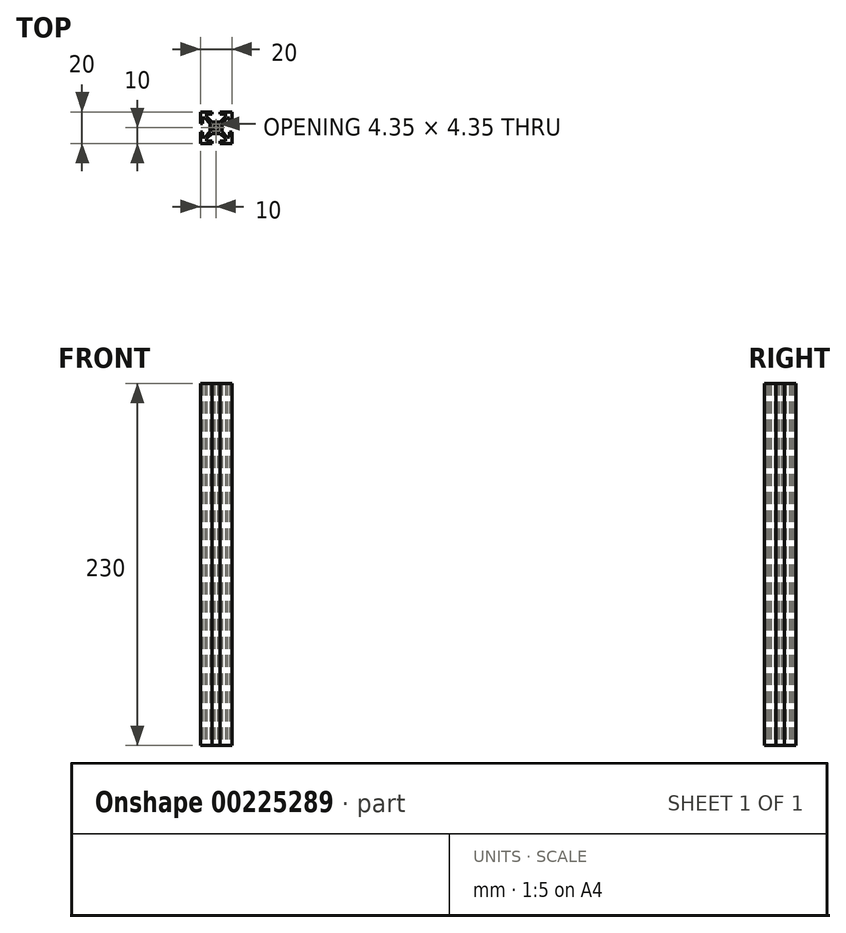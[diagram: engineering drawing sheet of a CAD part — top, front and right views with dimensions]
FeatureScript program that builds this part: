
annotation { "Feature Type Name" : "Feature", "Feature Type Description" : "" }
export const myFeature = defineFeature(function(context is Context, id is Id, definition is map)
    precondition{}
    {
        {
            var Q0;
            Q0=qCreatedBy(makeId("Top.planeOp"),FACE);
            var sketch = newSketch(context, id + "F0", { "sketchPlane" : qUnion([Q0])});
            skLineSegment(sketch, "E0.bottom", {"start": v(10, 10) * mm, "end": v(-10, 10) * mm});
            skLineSegment(sketch, "E0.top", {"start": v(10, -10) * mm, "end": v(-10, -10) * mm});
            skLineSegment(sketch, "E0.left", {"start": v(10, 10) * mm, "end": v(10, -10) * mm});
            skLineSegment(sketch, "E0.right", {"start": v(-10, 10) * mm, "end": v(-10, -10) * mm});
            skPoint(sketch, "E0.middle", {"position": v(0, 0) * mm});
            skLineSegment(sketch, "E1", {"start": v(-10, 10) * mm, "end": v(10, -10) * mm, "construction": true});
            skLineSegment(sketch, "E2", {"start": v(-10, -10) * mm, "end": v(10, 10) * mm, "construction": true});
            skLineSegment(sketch, "E3", {"start": v(0, 10) * mm, "end": v(0, -10) * mm, "construction": true});
            skLineSegment(sketch, "E4", {"start": v(-10, 0) * mm, "end": v(10, 0) * mm, "construction": true});
            skPoint(sketch, "E4.endSnap0", {"position": v(10, 0) * mm});
            skLineSegment(sketch, "E5", {"start": v(-2.63, 13.49) * mm, "end": v(2.63, 13.49) * mm});
            skLineSegment(sketch, "E6", {"start": v(2.63, 13.49) * mm, "end": v(2.63, 8.5) * mm});
            skLineSegment(sketch, "E7", {"start": v(2.63, 8.5) * mm, "end": v(6, 8.5) * mm});
            skLineSegment(sketch, "E8", {"start": v(6, 8.5) * mm, "end": v(6, 7.06) * mm});
            skLineSegment(sketch, "E9", {"start": v(6, 7.06) * mm, "end": v(2.6, 3.66) * mm});
            skLineSegment(sketch, "E10", {"start": v(2.6, 3.66) * mm, "end": v(-2.6, 3.66) * mm});
            skLineSegment(sketch, "E11", {"start": v(-2.6, 3.66) * mm, "end": v(-6, 7.06) * mm});
            skLineSegment(sketch, "E12", {"start": v(-6, 7.06) * mm, "end": v(-6, 8.5) * mm});
            skLineSegment(sketch, "E13", {"start": v(-6, 8.5) * mm, "end": v(-2.63, 8.5) * mm});
            skLineSegment(sketch, "E14", {"start": v(-2.63, 8.5) * mm, "end": v(-2.63, 13.49) * mm});
            skCircle(sketch, "E15", {"center": v(0, 0) * mm, "radius": 2.1 * mm});
            skLineSegment(sketch, "E16.MirrorCS", {"start": v(-7.06, 6) * mm, "end": v(-8.5, 6) * mm});
            skLineSegment(sketch, "E17.MirrorCS", {"start": v(-3.66, 2.6) * mm, "end": v(-7.06, 6) * mm});
            skLineSegment(sketch, "E18.MirrorCS", {"start": v(-8.5, 6) * mm, "end": v(-8.5, 2.63) * mm});
            skLineSegment(sketch, "E19.MirrorCS", {"start": v(-3.66, -2.6) * mm, "end": v(-3.66, 2.6) * mm});
            skLineSegment(sketch, "E20.MirrorCS", {"start": v(-7.06, -6) * mm, "end": v(-3.66, -2.6) * mm});
            skLineSegment(sketch, "E21.MirrorCS", {"start": v(-8.5, -6) * mm, "end": v(-7.06, -6) * mm});
            skLineSegment(sketch, "E22.MirrorCS", {"start": v(-8.5, -2.63) * mm, "end": v(-8.5, -6) * mm});
            skLineSegment(sketch, "E23.MirrorCS", {"start": v(-13.49, -2.63) * mm, "end": v(-8.5, -2.63) * mm});
            skLineSegment(sketch, "E24.MirrorCS", {"start": v(-13.49, 2.63) * mm, "end": v(-13.49, -2.63) * mm});
            skLineSegment(sketch, "E25.MirrorCS", {"start": v(-8.5, 2.63) * mm, "end": v(-13.49, 2.63) * mm});
            skLineSegment(sketch, "E26.MirrorCS", {"start": v(-2.6, -3.66) * mm, "end": v(-6, -7.06) * mm});
            skLineSegment(sketch, "E27.MirrorCS", {"start": v(2.6, -3.66) * mm, "end": v(-2.6, -3.66) * mm});
            skLineSegment(sketch, "E28.MirrorCS", {"start": v(6, -7.06) * mm, "end": v(2.6, -3.66) * mm});
            skLineSegment(sketch, "E29.MirrorCS", {"start": v(6, -8.5) * mm, "end": v(6, -7.06) * mm});
            skLineSegment(sketch, "E30.MirrorCS", {"start": v(2.63, -8.5) * mm, "end": v(6, -8.5) * mm});
            skLineSegment(sketch, "E31.MirrorCS", {"start": v(2.63, -13.49) * mm, "end": v(2.63, -8.5) * mm});
            skLineSegment(sketch, "E32.MirrorCS", {"start": v(-2.63, -13.49) * mm, "end": v(2.63, -13.49) * mm});
            skLineSegment(sketch, "E33.MirrorCS", {"start": v(-2.63, -8.5) * mm, "end": v(-2.63, -13.49) * mm});
            skLineSegment(sketch, "E34.MirrorCS", {"start": v(-6, -8.5) * mm, "end": v(-2.63, -8.5) * mm});
            skLineSegment(sketch, "E35.MirrorCS", {"start": v(-6, -7.06) * mm, "end": v(-6, -8.5) * mm});
            skLineSegment(sketch, "E36.MirrorCS", {"start": v(7.06, 6) * mm, "end": v(3.66, 2.6) * mm});
            skLineSegment(sketch, "E37.MirrorCS", {"start": v(8.5, 6) * mm, "end": v(7.06, 6) * mm});
            skLineSegment(sketch, "E38.MirrorCS", {"start": v(8.5, 2.63) * mm, "end": v(8.5, 6) * mm});
            skLineSegment(sketch, "E39.MirrorCS", {"start": v(13.49, 2.63) * mm, "end": v(8.5, 2.63) * mm});
            skLineSegment(sketch, "E40.MirrorCS", {"start": v(13.49, -2.63) * mm, "end": v(13.49, 2.63) * mm});
            skLineSegment(sketch, "E41.MirrorCS", {"start": v(8.5, -2.63) * mm, "end": v(13.49, -2.63) * mm});
            skLineSegment(sketch, "E42.MirrorCS", {"start": v(8.5, -6) * mm, "end": v(8.5, -2.63) * mm});
            skLineSegment(sketch, "E43.MirrorCS", {"start": v(7.06, -6) * mm, "end": v(8.5, -6) * mm});
            skLineSegment(sketch, "E44.MirrorCS", {"start": v(3.66, -2.6) * mm, "end": v(7.06, -6) * mm});
            skLineSegment(sketch, "E45.MirrorCS", {"start": v(3.66, 2.6) * mm, "end": v(3.66, -2.6) * mm});
            skCircle(sketch, "E46", {"center": v(-1.48, 1.48) * mm, "radius": 0.7 * mm});
            skCircle(sketch, "E47.MirrorC", {"center": v(1.48, 1.48) * mm, "radius": 0.7 * mm});
            skCircle(sketch, "E48.MirrorC", {"center": v(-1.48, -1.48) * mm, "radius": 0.7 * mm});
            skCircle(sketch, "E49.MirrorC", {"center": v(1.48, -1.48) * mm, "radius": 0.7 * mm});
            skSolve(sketch);
        }
        {
            var Q0;
            {var subQ29=sQuery(id+"F0.wireOp",EDGE,"E7");Q0=makeQuery(id+"F0.imprint","IMPRINT",FACE,{"disambiguationData":[TD([[makeQuery(id+"F0.imprint","IMPRINT",EDGE,{"derivedFrom":subQ29}),1.0]])]});}
            extrude(context, id + "F1", {"entities" : qUnion([Q0]), "depth" : 230 * mm});
        }
    });
